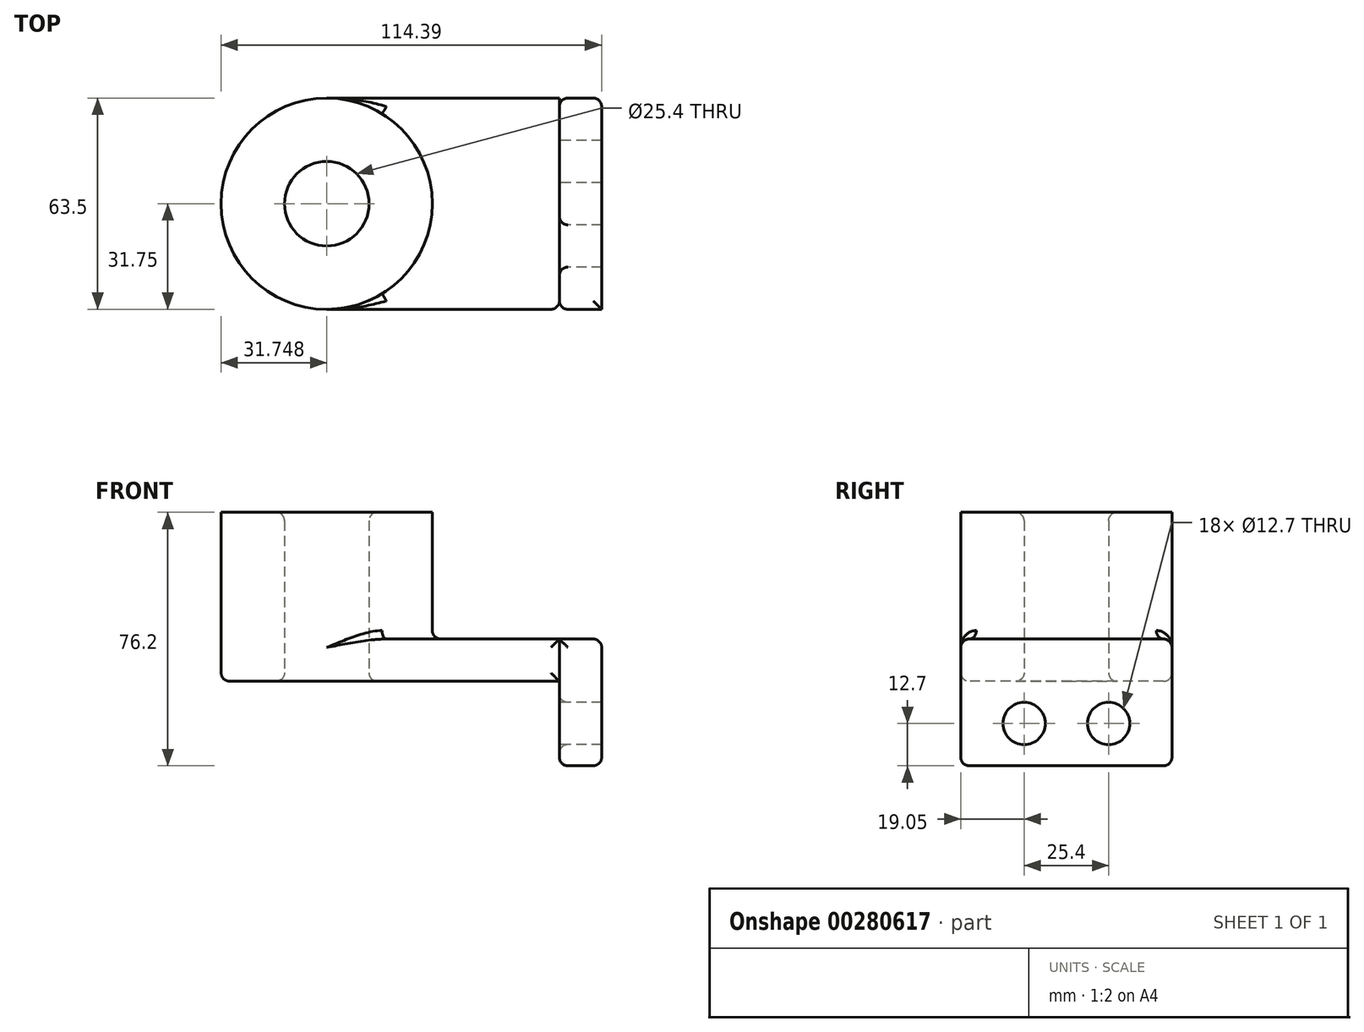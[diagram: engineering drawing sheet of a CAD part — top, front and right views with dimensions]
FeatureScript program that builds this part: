
annotation { "Feature Type Name" : "Feature", "Feature Type Description" : "" }
export const myFeature = defineFeature(function(context is Context, id is Id, definition is map)
    precondition{}
    {
        {
            var Q0;
            Q0=qCreatedBy(makeId("Top.planeOp"),FACE);
            var sketch = newSketch(context, id + "F0", { "sketchPlane" : qUnion([Q0])});
            skLineSegment(sketch, "E0.bottom", {"start": v(34.97, 31.75) * mm, "end": v(-34.97, 31.75) * mm});
            skLineSegment(sketch, "E0.top", {"start": v(34.97, -31.75) * mm, "end": v(-34.97, -31.75) * mm});
            skLineSegment(sketch, "E0.left", {"start": v(34.97, 31.75) * mm, "end": v(34.97, -31.75) * mm});
            skLineSegment(sketch, "E0.right", {"start": v(-34.97, 31.75) * mm, "end": v(-34.97, -31.75) * mm});
            skPoint(sketch, "E0.middle", {"position": v(0, 0) * mm});
            skCircle(sketch, "E1", {"center": v(-34.97, 0) * mm, "radius": 31.75 * mm});
            skCircle(sketch, "E2", {"center": v(-34.97, 0) * mm, "radius": 12.7 * mm});
            skSolve(sketch);
        }
        {
            var Q0;
            Q0 = qSketchRegion(id + "F0", true);
            extrude(context, id + "F1", {"entities" : qUnion([Q0]), "depth" : 12.7 * mm});
        }
        {
            var Q0;
            {var subQ1=sQuery(id+"F0.wireOp",EDGE,"E0.right");var subQ3=sQuery(id+"F0.wireOp",EDGE,"E2");var subQ4=makeQuery(id+"F0.imprint","INTERSECT",VERTEX,{"disambiguationData":[OD(0.0)],"derivedFrom":[subQ1,subQ3]});Q0=makeQuery(id+"F0.imprint","IMPRINT",FACE,{"disambiguationData":[TD([[makeQuery(id+"F0.imprint","IMPRINT",EDGE,{"disambiguationData":[TD([[subQ4,-1.0]])],"derivedFrom":subQ3}),-1.0]])]});}
            var Q1;
            {var subQ1=sQuery(id+"F0.wireOp",EDGE,"E0.right");var subQ3=sQuery(id+"F0.wireOp",EDGE,"E2");var subQ4=makeQuery(id+"F0.imprint","INTERSECT",VERTEX,{"disambiguationData":[OD(0.0)],"derivedFrom":[subQ1,subQ3]});Q1=makeQuery(id+"F0.imprint","IMPRINT",FACE,{"disambiguationData":[TD([[makeQuery(id+"F0.imprint","IMPRINT",EDGE,{"disambiguationData":[TD([[subQ4,1.0]])],"derivedFrom":subQ3}),-1.0]])]});}
            extrude(context, id + "F2", {"entities" : qUnion([Q0, Q1]), "operationType" : NewBodyOperationType.ADD, "depth" : 50.8 * mm});
        }
        {
            var Q0;
            Q0=makeQuery(id+"F1.opExtrude","SWEPT_FACE",FACE,{"disambiguationData":[OSD([sQuery(id+"F0.wireOp",EDGE,"E0.left")])]});
            var sketch = newSketch(context, id + "F3", { "sketchPlane" : qUnion([Q0])});
            skLineSegment(sketch, "E3.bottom", {"start": v(-31.75, 12.7) * mm, "end": v(31.75, 12.7) * mm});
            skLineSegment(sketch, "E3.top", {"start": v(-31.75, -25.4) * mm, "end": v(31.75, -25.4) * mm});
            skLineSegment(sketch, "E3.left", {"start": v(-31.75, 12.7) * mm, "end": v(-31.75, -25.4) * mm});
            skLineSegment(sketch, "E3.right", {"start": v(31.75, 12.7) * mm, "end": v(31.75, -25.4) * mm});
            skCircle(sketch, "E4", {"center": v(-12.7, -12.7) * mm, "radius": 6.35 * mm});
            skLineSegment(sketch, "E5", {"start": v(0, 0) * mm, "end": v(0, -25.4) * mm, "construction": true});
            skCircle(sketch, "E6.MirrorC", {"center": v(12.7, -12.7) * mm, "radius": 6.35 * mm});
            skSolve(sketch);
        }
        {
            var Q0;
            Q0 = qSketchRegion(id + "F3", true);
            extrude(context, id + "F4", {"entities" : qUnion([Q0]), "depth" : 12.7 * mm});
        }
        {
            var Q0;
            {var subQ0=sQuery(id+"F0.wireOp",EDGE,"E1");Q0=makeQuery(id+"F2.boolean.opBoolean","INTERSECT",EDGE,{"derivedFrom":[makeQuery(id+"F1.opExtrude","CAP_FACE",FACE,{"disambiguationData":[OSD([sQuery(id+"F0.wireOp",EDGE,"E0.bottom"),sQuery(id+"F0.wireOp",EDGE,"E0.top"),sQuery(id+"F0.wireOp",EDGE,"E0.left"),subQ0,sQuery(id+"F0.wireOp",EDGE,"E2")])],"isStart":false}),makeQuery(id+"F2.opExtrude","SWEPT_FACE",FACE,{"disambiguationData":[OSD([subQ0])]})]});}
            var Q1;
            Q1=makeQuery(id+"F4.opExtrude","CAP_EDGE",EDGE,{"disambiguationData":[OSD([sQuery(id+"F3.wireOp",EDGE,"E3.bottom")])],"isStart":false});
            var Q2;
            Q2=makeQuery(id+"F4.opExtrude","SWEPT_EDGE",EDGE,{"disambiguationData":[OSD([sQuery(id+"F3.wireOp",EDGE,"E3.top"),sQuery(id+"F3.wireOp",EDGE,"E3.right")])]});
            var Q3;
            Q3=makeQuery(id+"F4.opExtrude","SWEPT_EDGE",EDGE,{"disambiguationData":[OSD([sQuery(id+"F3.wireOp",EDGE,"E3.top"),sQuery(id+"F3.wireOp",EDGE,"E3.left")])]});
            var Q4;
            Q4=makeQuery(id+"F1.opExtrude","CAP_EDGE",EDGE,{"disambiguationData":[OSD([sQuery(id+"F0.wireOp",EDGE,"E0.bottom")])],"isStart":true});
            var Q5;
            Q5=makeQuery(id+"F4.opExtrude","CAP_EDGE",EDGE,{"disambiguationData":[OSD([sQuery(id+"F3.wireOp",EDGE,"E3.right")])],"isStart":true});
            var Q6;
            Q6=makeQuery(id+"F4.opExtrude","CAP_EDGE",EDGE,{"disambiguationData":[OSD([sQuery(id+"F3.wireOp",EDGE,"E3.right")])],"isStart":false});
            var Q7;
            Q7=makeQuery(id+"F4.opExtrude","CAP_EDGE",EDGE,{"disambiguationData":[OSD([sQuery(id+"F3.wireOp",EDGE,"E3.top")])],"isStart":true});
            var Q8;
            Q8=makeQuery(id+"F4.opExtrude","SWEPT_FACE",FACE,{"disambiguationData":[OSD([sQuery(id+"F3.wireOp",EDGE,"E3.top")])]});
            var Q9;
            Q9=makeQuery(id+"F4.opExtrude","SWEPT_EDGE",EDGE,{"disambiguationData":[OSD([sQuery(id+"F3.wireOp",EDGE,"E3.bottom"),sQuery(id+"F3.wireOp",EDGE,"E3.right")])]});
            var Q10;
            Q10=makeQuery(id+"F1.opExtrude","CAP_EDGE",EDGE,{"disambiguationData":[OSD([sQuery(id+"F0.wireOp",EDGE,"E0.bottom")])],"isStart":false});
            var Q11;
            Q11=makeQuery(id+"F4.opExtrude","SWEPT_EDGE",EDGE,{"disambiguationData":[OSD([sQuery(id+"F3.wireOp",EDGE,"E3.bottom"),sQuery(id+"F3.wireOp",EDGE,"E3.left")])]});
            var Q12;
            Q12=makeQuery(id+"F1.opExtrude","CAP_EDGE",EDGE,{"disambiguationData":[OSD([sQuery(id+"F0.wireOp",EDGE,"E0.top")])],"isStart":false});
            var Q13;
            Q13=makeQuery(id+"F1.opExtrude","SWEPT_EDGE",EDGE,{"disambiguationData":[OSD([sQuery(id+"F0.wireOp",EDGE,"E0.top"),sQuery(id+"F0.wireOp",EDGE,"E0.left")])]});
            var Q14;
            Q14=makeQuery(id+"F4.opExtrude","CAP_EDGE",EDGE,{"disambiguationData":[OSD([sQuery(id+"F3.wireOp",EDGE,"E4")])],"isStart":true});
            var Q15;
            Q15=makeQuery(id+"F1.opExtrude","CAP_EDGE",EDGE,{"disambiguationData":[OSD([sQuery(id+"F0.wireOp",EDGE,"E0.top")])],"isStart":true});
            var Q16;
            Q16=makeQuery(id+"F4.opExtrude","CAP_EDGE",EDGE,{"disambiguationData":[OSD([sQuery(id+"F3.wireOp",EDGE,"E3.left")])],"isStart":true});
            var Q17;
            Q17=makeQuery(id+"F1.opExtrude","CAP_EDGE",EDGE,{"disambiguationData":[OSD([sQuery(id+"F0.wireOp",EDGE,"E2")])],"isStart":true});
            var Q18;
            Q18=makeQuery(id+"F2.opExtrude","CAP_EDGE",EDGE,{"disambiguationData":[OSD([sQuery(id+"F0.wireOp",EDGE,"E2")])],"isStart":false});
            fillet(context, id + "F5", {"entities" : qUnion([Q0, Q1, Q2, Q3, Q4, Q5, Q6, Q7, Q8, Q9, Q10, Q11, Q12, Q13, Q14, Q15, Q16, Q17, Q18]), "radius" : 2.54 * mm, "tangentPropagation" : true, "allowEdgeOverflow" : false});
        }
    });
